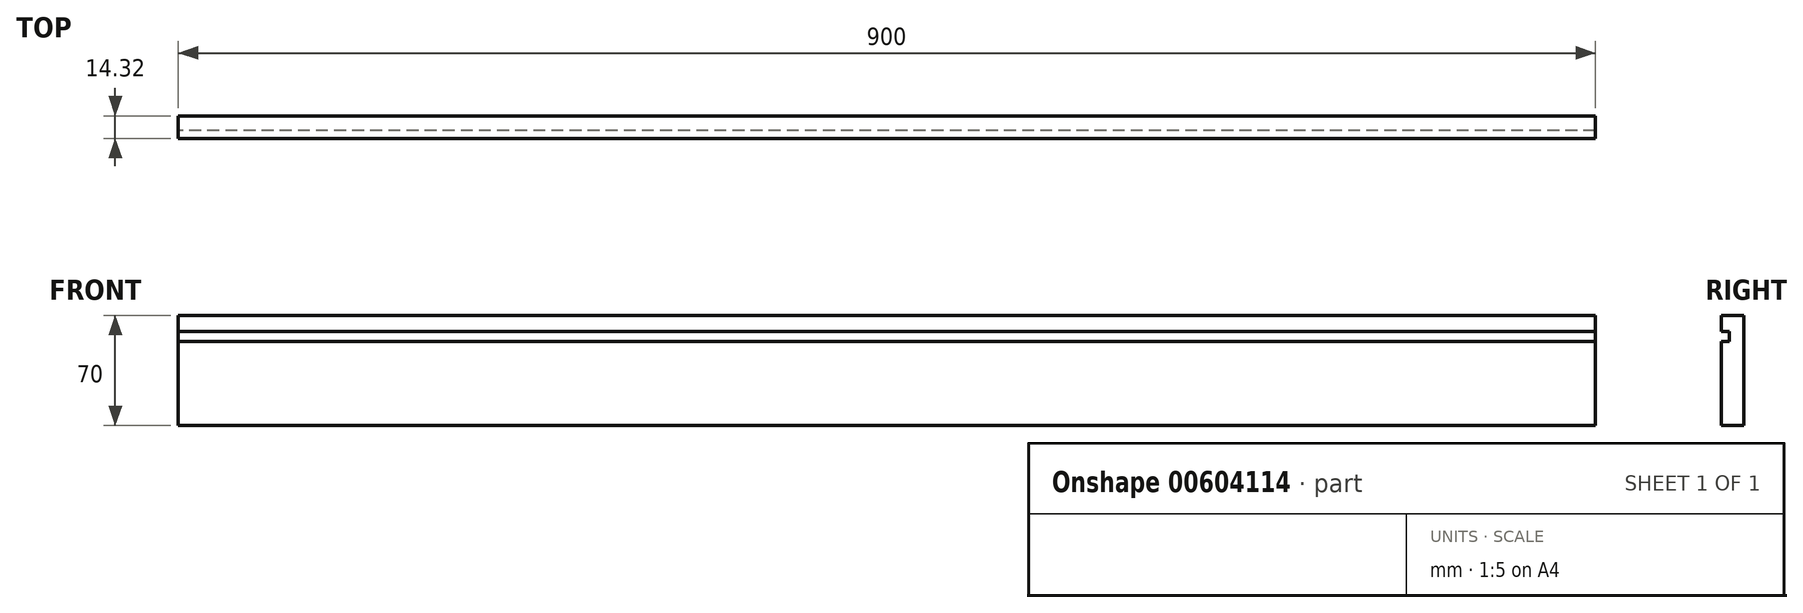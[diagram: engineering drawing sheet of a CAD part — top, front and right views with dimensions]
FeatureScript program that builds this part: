
annotation { "Feature Type Name" : "Feature", "Feature Type Description" : "" }
export const myFeature = defineFeature(function(context is Context, id is Id, definition is map)
    precondition{}
    {
        {
            var Q0;
            Q0=qCreatedBy(makeId("Right.planeOp"),FACE);
            var sketch = newSketch(context, id + "F0", { "sketchPlane" : qUnion([Q0])});
            skLineSegment(sketch, "E0", {"start": v(0, 0) * mm, "end": v(0, 70) * mm});
            skLineSegment(sketch, "E1", {"start": v(-14.32, 0) * mm, "end": v(-14.32, 53.58) * mm});
            skLineSegment(sketch, "E2", {"start": v(-14.32, 53.58) * mm, "end": v(-9.32, 53.58) * mm});
            skLineSegment(sketch, "E3", {"start": v(-9.32, 53.58) * mm, "end": v(-9.32, 59.75) * mm});
            skLineSegment(sketch, "E4", {"start": v(-9.32, 59.75) * mm, "end": v(-14.32, 59.75) * mm});
            skLineSegment(sketch, "E5", {"start": v(-14.32, 59.75) * mm, "end": v(-14.32, 70) * mm});
            skLineSegment(sketch, "E6", {"start": v(-14.32, 70) * mm, "end": v(0, 70) * mm});
            skLineSegment(sketch, "E7", {"start": v(0, 79) * mm, "end": v(-12, 79) * mm});
            skLineSegment(sketch, "E8", {"start": v(-14.32, 70) * mm, "end": v(-14.32, 79) * mm});
            skLineSegment(sketch, "E9", {"start": v(0, 0) * mm, "end": v(-14.32, 0) * mm});
            skSolve(sketch);
        }
        {
            var Q0;
            Q0 = qSketchRegion(id + "F0", true);
            extrude(context, id + "F1", {"entities" : qUnion([Q0]), "depth" : 900 * mm, "offsetDistance" : 25 * mm});
        }
    });
